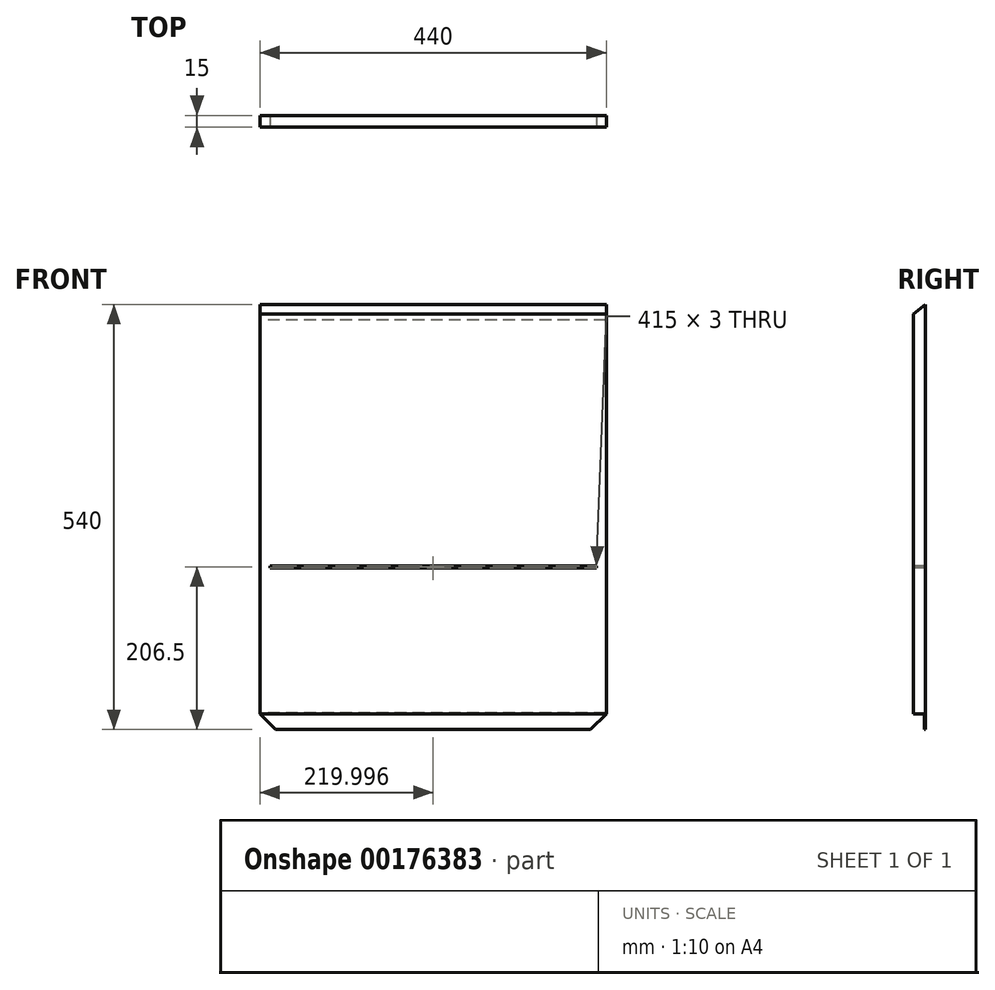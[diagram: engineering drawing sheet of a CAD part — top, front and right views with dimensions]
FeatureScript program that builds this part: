
annotation { "Feature Type Name" : "Feature", "Feature Type Description" : "" }
export const myFeature = defineFeature(function(context is Context, id is Id, definition is map)
    precondition{}
    {
        {
            var Q0;
            Q0=qCreatedBy(makeId("Front.planeOp"),FACE);
            var sketch = newSketch(context, id + "F0", { "sketchPlane" : qUnion([Q0])});
            skLineSegment(sketch, "E0.bottom", {"start": v(226.29, 260) * mm, "end": v(-213.71, 260) * mm});
            skLineSegment(sketch, "E0.top", {"start": v(226.29, -260) * mm, "end": v(-213.71, -260) * mm});
            skLineSegment(sketch, "E0.left", {"start": v(226.29, 260) * mm, "end": v(226.29, -260) * mm});
            skLineSegment(sketch, "E0.right", {"start": v(-213.71, 260) * mm, "end": v(-213.71, -260) * mm});
            skPoint(sketch, "E0.middle", {"position": v(6.29, 0) * mm});
            skSolve(sketch);
        }
        {
            var Q0;
            Q0 = qSketchRegion(id + "F0", true);
            extrude(context, id + "F1", {"entities" : qUnion([Q0]), "depth" : 15 * mm});
        }
        {
            var Q0;
            Q0=makeQuery(id+"F1.opExtrude","SWEPT_FACE",FACE,{"disambiguationData":[OSD([sQuery(id+"F0.wireOp",EDGE,"E0.top")])]});
            var sketch = newSketch(context, id + "F2", { "sketchPlane" : qUnion([Q0])});
            skLineSegment(sketch, "E1.bottom", {"start": v(-213.71, 0) * mm, "end": v(226.29, 0) * mm});
            skLineSegment(sketch, "E1.top", {"start": v(-213.71, 1) * mm, "end": v(226.29, 1) * mm});
            skLineSegment(sketch, "E1.left", {"start": v(-213.71, 0) * mm, "end": v(-213.71, 1) * mm});
            skLineSegment(sketch, "E1.right", {"start": v(226.29, 0) * mm, "end": v(226.29, 1) * mm});
            skSolve(sketch);
        }
        {
            var Q0;
            Q0 = qSketchRegion(id + "F2", true);
            extrude(context, id + "F3", {"entities" : qUnion([Q0]), "operationType" : NewBodyOperationType.ADD, "depth" : 20 * mm});
        }
        {
            var Q0;
            Q0=makeQuery(id+"F1.opExtrude","CAP_EDGE",EDGE,{"disambiguationData":[OSD([sQuery(id+"F0.wireOp",EDGE,"E0.bottom")])],"isStart":false});
            chamfer(context, id + "F4", {"entities" : qUnion([Q0]), "chamferType" : ChamferType.TWO_OFFSETS, "width1" : 12.5 * mm, "oppositeDirection" : false, "width2" : 15 * mm, "tangentPropagation" : true});
        }
        {
            var Q0;
            Q0=makeQuery(id+"F3.opExtrude","CAP_EDGE",EDGE,{"disambiguationData":[OSD([sQuery(id+"F2.wireOp",EDGE,"E1.left")])],"isStart":false});
            var Q1;
            Q1=makeQuery(id+"F3.opExtrude","CAP_EDGE",EDGE,{"disambiguationData":[OSD([sQuery(id+"F2.wireOp",EDGE,"E1.right")])],"isStart":false});
            chamfer(context, id + "F5", {"entities" : qUnion([Q0, Q1]), "width" : 20 * mm, "tangentPropagation" : true});
        }
        {
            var Q0;
            Q0=makeQuery(id+"F3.boolean.opBoolean","MERGE",FACE,{"derivedFrom":[makeQuery(id+"F1.opExtrude","CAP_FACE",FACE,{"disambiguationData":[OSD([sQuery(id+"F0.wireOp",EDGE,"E0.bottom"),sQuery(id+"F0.wireOp",EDGE,"E0.top"),sQuery(id+"F0.wireOp",EDGE,"E0.left"),sQuery(id+"F0.wireOp",EDGE,"E0.right")])],"isStart":true}),makeQuery(id+"F3.opExtrude","SWEPT_FACE",FACE,{"disambiguationData":[OSD([sQuery(id+"F2.wireOp",EDGE,"E1.bottom")])]})]});
            var sketch = newSketch(context, id + "F6", { "sketchPlane" : qUnion([Q0])});
            skLineSegment(sketch, "E2.bottom", {"start": v(-225.29, 240) * mm, "end": v(212.71, 240) * mm});
            skLineSegment(sketch, "E2.top", {"start": v(-225.29, -259) * mm, "end": v(212.71, -259) * mm});
            skLineSegment(sketch, "E2.left", {"start": v(-225.29, 240) * mm, "end": v(-225.29, -259) * mm});
            skLineSegment(sketch, "E2.right", {"start": v(212.71, 240) * mm, "end": v(212.71, -259) * mm});
            skSolve(sketch);
        }
        {
            var Q0;
            Q0 = qSketchRegion(id + "F6", true);
            extrude(context, id + "F7", {"entities" : qUnion([Q0]), "operationType" : NewBodyOperationType.REMOVE, "oppositeDirection" : true, "depth" : 1 * mm});
        }
        {
            var Q0;
            Q0=makeQuery(id+"F1.opExtrude","CAP_FACE",FACE,{"disambiguationData":[OSD([sQuery(id+"F0.wireOp",EDGE,"E0.bottom"),sQuery(id+"F0.wireOp",EDGE,"E0.top"),sQuery(id+"F0.wireOp",EDGE,"E0.left"),sQuery(id+"F0.wireOp",EDGE,"E0.right")])],"isStart":false});
            var sketch = newSketch(context, id + "F8", { "sketchPlane" : qUnion([Q0])});
            skLineSegment(sketch, "E3.bottom", {"start": v(-201.21, -72) * mm, "end": v(213.79, -72) * mm});
            skLineSegment(sketch, "E3.top", {"start": v(-201.21, -75) * mm, "end": v(213.79, -75) * mm});
            skLineSegment(sketch, "E3.left", {"start": v(-201.21, -72) * mm, "end": v(-201.21, -75) * mm});
            skLineSegment(sketch, "E3.right", {"start": v(213.79, -72) * mm, "end": v(213.79, -75) * mm});
            skSolve(sketch);
        }
        {
            var Q0;
            Q0 = qSketchRegion(id + "F8", true);
            extrude(context, id + "F9", {"entities" : qUnion([Q0]), "operationType" : NewBodyOperationType.REMOVE, "endBound" : BoundingType.THROUGH_ALL, "oppositeDirection" : true, "depth" : 25 * mm});
        }
    });
